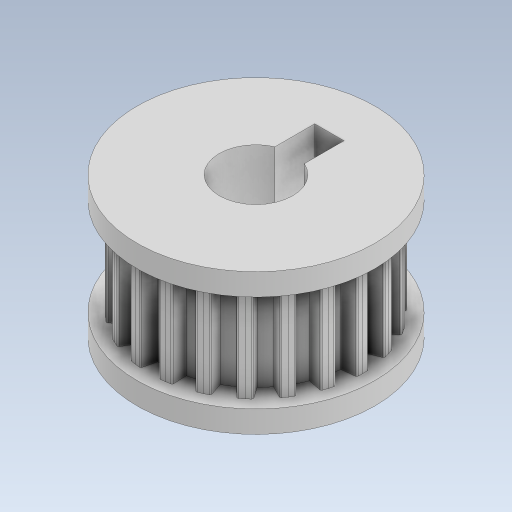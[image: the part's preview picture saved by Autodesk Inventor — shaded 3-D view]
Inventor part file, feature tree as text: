
AUTODESK INVENTOR PART (.ipt)
format: ipt  version: 2023.5 (Build 275446000, 446)  size: 801,792 bytes
history: native  units: mm
features: extrude x5, sketch x4, projected_geometry x3, pattern_circular x1
ambient origin geometry x8: Origin, YZ Plane, XZ Plane, XY Plane, X Axis, Y Axis, Z Axis, Center Point
bodies: Solid1 (feature_tree)
feature tree (13):
  sketch  "Sketch1"  dims[d0=5.0mm d2=14.55mm]
  extrude  "Extrusion1"  Depth=14.55mm
  extrude  "Extrusion2"  Depth=0.4mm
  pattern_circular  "Circular Pattern1"  [2 undecoded]
  extrude  "Extrusion3"  Depth=10.0mm TaperAngle=360.0deg
  extrude  "Extrusion4"  Depth=10.0mm
  extrude  "Extrusion6"  Depth=1.5mm TaperAngle=0.0deg
  sketch  "Sketch2"  dims[d3=12.6mm d4=0.4mm]
  sketch  "Sketch3"  dims[d5=0.1mm]
  sketch  "Sketch5"  dims[d6=6.6mm d7=0.0mm d8=6.6mm d9=0.0mm d10=220.0mm d11=360.0deg d13=16.2mm d14=1.5mm d15=0.0mm d16=1.5mm d17=0.0mm d20=16.2mm d21=5.0mm d22=5.0mm d23=5.0mm d24=10.0mm d25=0.0mm d26=14.55mm d18=0.5mm d19=0.872665mm]
  projected_geometry  "Projected Loop1"
  projected_geometry  "Projected Loop2"
  projected_geometry  "Projected Loop3"
note: 2 required parameter values undecoded (feature->parameter linkage not recoverable at this tier; creation-order binding heuristic only, values carry confidence <= 0.55)
